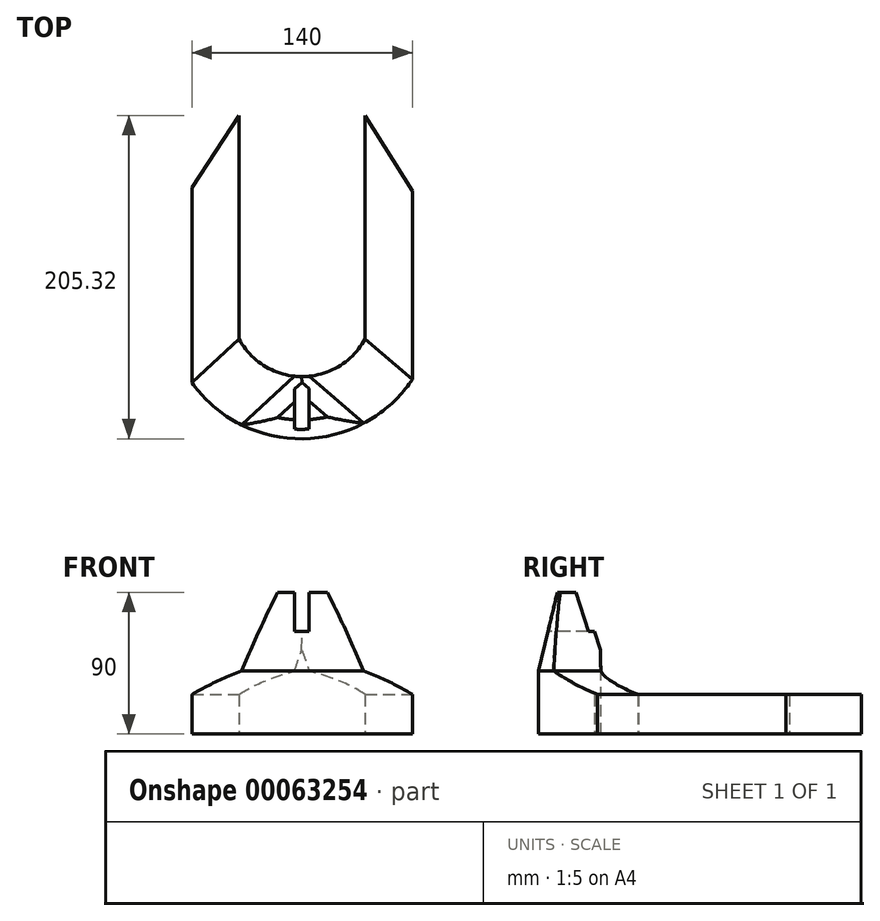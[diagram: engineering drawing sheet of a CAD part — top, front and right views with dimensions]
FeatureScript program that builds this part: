
annotation { "Feature Type Name" : "Feature", "Feature Type Description" : "" }
export const myFeature = defineFeature(function(context is Context, id is Id, definition is map)
    precondition{}
    {
        {
            var Q0;
            Q0=qCreatedBy(makeId("Top.planeOp"),FACE);
            var sketch = newSketch(context, id + "F0", { "sketchPlane" : qUnion([Q0])});
            skLineSegment(sketch, "E0", {"start": v(-70, 60.34) * mm, "end": v(-70, -63.68) * mm});
            skLineSegment(sketch, "E1", {"start": v(70, 58.02) * mm, "end": v(70, -61.64) * mm});
            skLineSegment(sketch, "E2", {"start": v(-40, 106) * mm, "end": v(-40, -36) * mm});
            skLineSegment(sketch, "E3", {"start": v(40, -35.8) * mm, "end": v(40, 106) * mm});
            skArc(sketch, "E4", {"start": v(-40, -36) * mm, "mid": v(0.06, -59.8) * mm, "end": v(40, -35.8) * mm});
            skLineSegment(sketch, "E5", {"start": v(-70, 60.34) * mm, "end": v(-40, 106) * mm});
            skLineSegment(sketch, "E6", {"start": v(40, 106) * mm, "end": v(70, 58.02) * mm});
            skArc(sketch, "E7", {"start": v(-70, -63.68) * mm, "mid": v(0.53, -99.3) * mm, "end": v(70, -61.64) * mm});
            skLineSegment(sketch, "E8", {"start": v(-40, -36) * mm, "end": v(-70, -63.68) * mm});
            skLineSegment(sketch, "E9", {"start": v(40, -35.8) * mm, "end": v(70, -61.64) * mm});
            skSolve(sketch);
        }
        {
            var Q0;
            Q0=makeQuery(id+"F0.imprint","IMPRINT",FACE,{"disambiguationData":[TD([[makeQuery(id+"F0.imprint","IMPRINT",EDGE,{"derivedFrom":sQuery(id+"F0.wireOp",EDGE,"E4")}),-1.0]])]});
            extrude(context, id + "F1", {"entities" : qUnion([Q0]), "depth" : 40 * mm});
        }
        {
            var Q0;
            Q0=makeQuery(id+"F0.imprint","IMPRINT",FACE,{"disambiguationData":[TD([[makeQuery(id+"F0.imprint","IMPRINT",EDGE,{"derivedFrom":sQuery(id+"F0.wireOp",EDGE,"E0")}),1.0]])]});
            extrude(context, id + "F2", {"entities" : qUnion([Q0]), "operationType" : NewBodyOperationType.ADD, "depth" : 25 * mm});
        }
        {
            var Q0;
            Q0=makeQuery(id+"F0.imprint","IMPRINT",FACE,{"disambiguationData":[TD([[makeQuery(id+"F0.imprint","IMPRINT",EDGE,{"derivedFrom":sQuery(id+"F0.wireOp",EDGE,"E1")}),-1.0]])]});
            extrude(context, id + "F3", {"entities" : qUnion([Q0]), "operationType" : NewBodyOperationType.ADD, "depth" : 25 * mm});
        }
        {
            var Q0;
            Q0=makeQuery(id+"F1.opExtrude","CAP_EDGE",EDGE,{"disambiguationData":[OSD([sQuery(id+"F0.wireOp",EDGE,"E9")])],"isStart":false});
            var Q1;
            Q1=makeQuery(id+"F1.opExtrude","CAP_EDGE",EDGE,{"disambiguationData":[OSD([sQuery(id+"F0.wireOp",EDGE,"E8")])],"isStart":false});
            chamfer(context, id + "F4", {"entities" : qUnion([Q0, Q1]), "chamferType" : ChamferType.OFFSET_ANGLE, "width" : 15 * mm, "oppositeDirection" : false, "angle" : 70 * degree, "tangentPropagation" : true});
        }
        {
            var Q0;
            Q0=makeQuery(id+"F1.opExtrude","CAP_FACE",FACE,{"disambiguationData":[OSD([sQuery(id+"F0.wireOp",EDGE,"E4"),sQuery(id+"F0.wireOp",EDGE,"E7"),sQuery(id+"F0.wireOp",EDGE,"E8"),sQuery(id+"F0.wireOp",EDGE,"E9")])],"isStart":false});
            extrude(context, id + "F5", {"entities" : qUnion([Q0]), "operationType" : NewBodyOperationType.ADD, "depth" : 25 * mm});
        }
        {
            var Q0;
            Q0=makeQuery(id+"F5.opExtrude","CAP_FACE",FACE,{"disambiguationData":[OSD([sQuery(id+"F0.wireOp",EDGE,"E4"),sQuery(id+"F0.wireOp",EDGE,"E7"),sQuery(id+"F0.wireOp",EDGE,"E8"),sQuery(id+"F0.wireOp",EDGE,"E9")])],"isStart":false});
            var sketch = newSketch(context, id + "F6", { "sketchPlane" : qUnion([Q0])});
            skLineSegment(sketch, "E10", {"start": v(-4.75, -59.55) * mm, "end": v(-4.75, -99.3) * mm});
            skPoint(sketch, "E10.endSnap0", {"position": v(0.52, -99.3) * mm});
            skLineSegment(sketch, "E11", {"start": v(4.46, -59.57) * mm, "end": v(4.46, -99.16) * mm});
            skSolve(sketch);
        }
        {
            var Q0;
            {var subQ1=sQuery(id+"F0.wireOp",EDGE,"E9");var subQ2=sQuery(id+"F0.wireOp",EDGE,"E8");var subQ3=sQuery(id+"F0.wireOp",EDGE,"E7");var subQ4=sQuery(id+"F0.wireOp",EDGE,"E4");var subQ5=makeQuery(id+"F5.opExtrude","CAP_EDGE",EDGE,{"disambiguationData":[OSD([subQ4,subQ3,subQ2,subQ1]),TDD([makeQuery(id+"F4.opChamfer","BLEND_EDGE",EDGE,{"blendedFrom":[makeQuery(id+"F1.opExtrude","CAP_EDGE",EDGE,{"disambiguationData":[OSD([subQ2])],"isStart":false}),makeQuery(id+"F1.opExtrude","CAP_FACE",FACE,{"disambiguationData":[OSD([subQ4,subQ3,subQ2,subQ1])],"isStart":false})],"blendedInto":[makeQuery(id+"F1.opExtrude","CAP_FACE",FACE,{"disambiguationData":[OSD([subQ4,subQ3,subQ2,subQ1])],"isStart":false})]})])],"isStart":false});Q0=makeQuery(id+"F6.imprint","IMPRINT",FACE,{"disambiguationData":[TD([[makeQuery(id+"F6.imprint","IMPRINT",EDGE,{"derivedFrom":subQ5}),1.0]])]});}
            extrude(context, id + "F7", {"entities" : qUnion([Q0]), "operationType" : NewBodyOperationType.ADD, "depth" : 25 * mm});
        }
        {
            var Q0;
            {var subQ0=sQuery(id+"F6.wireOp",EDGE,"E11");Q0=makeQuery(id+"F6.imprint","IMPRINT",FACE,{"disambiguationData":[TD([[makeQuery(id+"F6.imprint","IMPRINT",EDGE,{"derivedFrom":subQ0}),1.0]])]});}
            extrude(context, id + "F8", {"entities" : qUnion([Q0]), "operationType" : NewBodyOperationType.ADD, "depth" : 25 * mm});
        }
        {
            var Q0;
            Q0=makeQuery(id+"F7.opExtrude","CAP_EDGE",EDGE,{"disambiguationData":[OSD([sQuery(id+"F0.wireOp",EDGE,"E7")])],"isStart":false});
            var Q1;
            Q1=makeQuery(id+"F7.opExtrude","CAP_EDGE",EDGE,{"disambiguationData":[OSD([sQuery(id+"F0.wireOp",EDGE,"E4"),sQuery(id+"F0.wireOp",EDGE,"E7"),sQuery(id+"F0.wireOp",EDGE,"E8"),sQuery(id+"F0.wireOp",EDGE,"E9")])],"isStart":false});
            var Q2;
            Q2=makeQuery(id+"F8.opExtrude","CAP_EDGE",EDGE,{"disambiguationData":[OSD([sQuery(id+"F0.wireOp",EDGE,"E7")])],"isStart":false});
            var Q3;
            Q3=makeQuery(id+"F8.opExtrude","CAP_EDGE",EDGE,{"disambiguationData":[OSD([sQuery(id+"F0.wireOp",EDGE,"E4"),sQuery(id+"F0.wireOp",EDGE,"E7"),sQuery(id+"F0.wireOp",EDGE,"E8"),sQuery(id+"F0.wireOp",EDGE,"E9")])],"isStart":false});
            chamfer(context, id + "F9", {"entities" : qUnion([Q0, Q1, Q2, Q3]), "chamferType" : ChamferType.OFFSET_ANGLE, "width" : 12 * mm, "oppositeDirection" : false, "angle" : 76.5 * degree, "tangentPropagation" : true});
        }
    });
